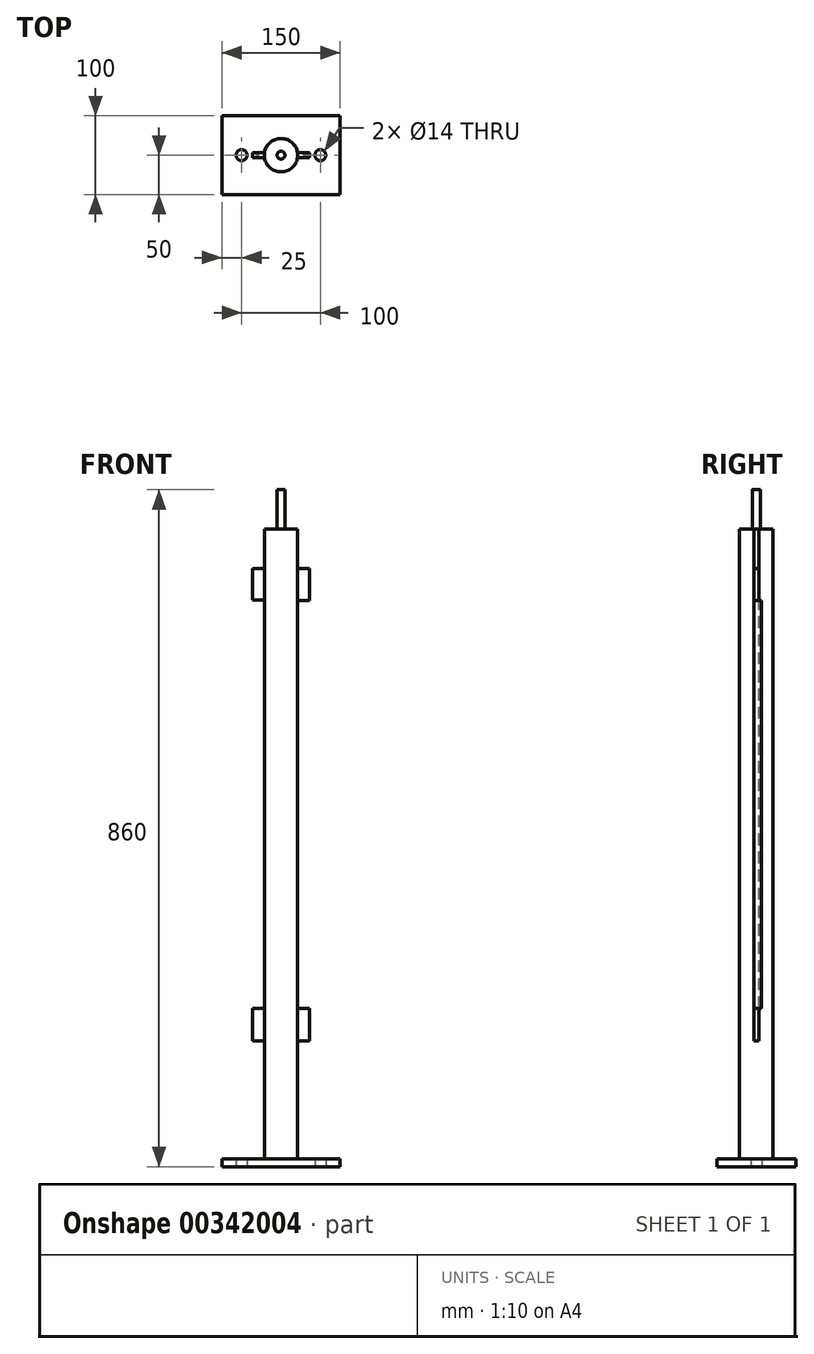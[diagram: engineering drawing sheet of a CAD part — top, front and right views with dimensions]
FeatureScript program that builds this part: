
annotation { "Feature Type Name" : "Feature", "Feature Type Description" : "" }
export const myFeature = defineFeature(function(context is Context, id is Id, definition is map)
    precondition{}
    {
        {
            var Q0;
            Q0=qCreatedBy(makeId("Top.planeOp"),FACE);
            var sketch = newSketch(context, id + "F0", { "sketchPlane" : qUnion([Q0])});
            skCircle(sketch, "E0", {"center": v(0, 0) * mm, "radius": 21.2 * mm});
            skSolve(sketch);
        }
        {
            var Q0;
            Q0 = qSketchRegion(id + "F0", true);
            extrude(context, id + "F1", {"entities" : qUnion([Q0]), "depth" : 800 * mm});
        }
        {
            var Q0;
            Q0=makeQuery(id+"F1.opExtrude","CAP_FACE",FACE,{"disambiguationData":[OSD([sQuery(id+"F0.wireOp",EDGE,"E0")])],"isStart":false});
            var sketch = newSketch(context, id + "F2", { "sketchPlane" : qUnion([Q0])});
            skCircle(sketch, "E1", {"center": v(0, 0) * mm, "radius": 5 * mm});
            skSolve(sketch);
        }
        {
            var Q0;
            Q0 = qSketchRegion(id + "F2", true);
            extrude(context, id + "F3", {"entities" : qUnion([Q0]), "operationType" : NewBodyOperationType.ADD, "depth" : 50 * mm});
        }
        {
            var Q0;
            Q0=makeQuery(id+"F1.opExtrude","CAP_FACE",FACE,{"disambiguationData":[OSD([sQuery(id+"F0.wireOp",EDGE,"E0")])],"isStart":true});
            var sketch = newSketch(context, id + "F4", { "sketchPlane" : qUnion([Q0])});
            skLineSegment(sketch, "E2.bottom", {"start": v(-75, -50) * mm, "end": v(75, -50) * mm});
            skLineSegment(sketch, "E2.top", {"start": v(-75, 50) * mm, "end": v(75, 50) * mm});
            skLineSegment(sketch, "E2.left", {"start": v(-75, -50) * mm, "end": v(-75, 50) * mm});
            skLineSegment(sketch, "E2.right", {"start": v(75, -50) * mm, "end": v(75, 50) * mm});
            skPoint(sketch, "E2.middle", {"position": v(0, 0) * mm});
            skSolve(sketch);
        }
        {
            var Q0;
            Q0 = qSketchRegion(id + "F4", true);
            extrude(context, id + "F5", {"entities" : qUnion([Q0]), "operationType" : NewBodyOperationType.ADD, "depth" : 10 * mm});
        }
        {
            var Q0;
            Q0=makeQuery(id+"F5.opExtrude","CAP_FACE",FACE,{"disambiguationData":[OSD([sQuery(id+"F4.wireOp",EDGE,"E2.bottom"),sQuery(id+"F4.wireOp",EDGE,"E2.top"),sQuery(id+"F4.wireOp",EDGE,"E2.left"),sQuery(id+"F4.wireOp",EDGE,"E2.right")])],"isStart":false});
            var sketch = newSketch(context, id + "F6", { "sketchPlane" : qUnion([Q0])});
            skLineSegment(sketch, "E3", {"start": v(-75, 0) * mm, "end": v(-50, 0) * mm});
            skLineSegment(sketch, "E4", {"start": v(75, 0) * mm, "end": v(50, 0) * mm});
            skPoint(sketch, "E4.endSnap0", {"position": v(75, 0) * mm});
            skSolve(sketch);
        }
        {
            var Q0;
            Q0=sQuery(id+"F6.wireOp",VERTEX,"E3.end");
            var Q1;
            Q1=sQuery(id+"F6.wireOp",VERTEX,"E4.end");
            var Q2;
            Q2=makeQuery(id+"F1.opExtrude","SWEPT_BODY",BODY,{"disambiguationData":[OSD([sQuery(id+"F0.wireOp",EDGE,"E0")])]});
            hole(context, id + "F7", {"style" : HoleStyle.SIMPLE, "endStyle" : HoleEndStyle.THROUGH, "holeDiameter" : 14 * mm, "isTappedThrough" : true, "tappedDepth" : 12 * mm, "tapClearance" : 3, "locations" : qUnion([Q0, Q1]), "scope" : qUnion([Q2])});
        }
        {
            var Q0;
            Q0=makeQuery(id+"F1.opExtrude","CAP_FACE",FACE,{"disambiguationData":[OSD([sQuery(id+"F0.wireOp",EDGE,"E0")])],"isStart":false});
            var sketch = newSketch(context, id + "F8", { "sketchPlane" : qUnion([Q0])});
            skLineSegment(sketch, "E5", {"start": v(36.2, 0) * mm, "end": v(36.2, 3) * mm});
            skLineSegment(sketch, "E6", {"start": v(36.2, 3) * mm, "end": v(20.99, 3) * mm});
            skLineSegment(sketch, "E7", {"start": v(36.2, 0) * mm, "end": v(36.2, -3) * mm});
            skLineSegment(sketch, "E8", {"start": v(36.2, -3) * mm, "end": v(20.99, -3) * mm});
            skLineSegment(sketch, "E9", {"start": v(20.99, -3) * mm, "end": v(20.99, 3) * mm});
            skLineSegment(sketch, "E10", {"start": v(-36.2, 0) * mm, "end": v(-36.2, 3) * mm});
            skLineSegment(sketch, "E11", {"start": v(-36.2, 3) * mm, "end": v(-20.99, 3) * mm});
            skLineSegment(sketch, "E12", {"start": v(-36.2, 0) * mm, "end": v(-36.2, -3) * mm});
            skLineSegment(sketch, "E13", {"start": v(-36.2, -3) * mm, "end": v(-20.99, -3) * mm});
            skLineSegment(sketch, "E14", {"start": v(-20.99, -3) * mm, "end": v(-20.99, 3) * mm});
            skSolve(sketch);
        }
        {
            var Q0;
            Q0 = qSketchRegion(id + "F8", true);
            extrude(context, id + "F9", {"entities" : qUnion([Q0]), "operationType" : NewBodyOperationType.ADD, "oppositeDirection" : true, "depth" : 650 * mm});
        }
        {
            var Q0;
            Q0=makeQuery(id+"F9.opExtrude","SWEPT_FACE",FACE,{"disambiguationData":[OSD([sQuery(id+"F8.wireOp",EDGE,"E13")])]});
            var sketch = newSketch(context, id + "F10", { "sketchPlane" : qUnion([Q0])});
            skLineSegment(sketch, "E15.bottom", {"start": v(-20.99, 800) * mm, "end": v(-39.72, 800) * mm});
            skLineSegment(sketch, "E15.top", {"start": v(-20.99, 750) * mm, "end": v(-39.72, 750) * mm});
            skLineSegment(sketch, "E15.left", {"start": v(-20.99, 800) * mm, "end": v(-20.99, 750) * mm});
            skLineSegment(sketch, "E15.right", {"start": v(-39.72, 800) * mm, "end": v(-39.72, 750) * mm});
            skPoint(sketch, "E16.oppositeSnap0", {"position": v(-30.35, 750) * mm});
            skLineSegment(sketch, "E16.bottom", {"start": v(21.1, 800) * mm, "end": v(39.26, 800) * mm});
            skLineSegment(sketch, "E16.top", {"start": v(21.1, 750) * mm, "end": v(39.26, 750) * mm});
            skLineSegment(sketch, "E16.left", {"start": v(21.1, 800) * mm, "end": v(21.1, 750) * mm});
            skLineSegment(sketch, "E16.right", {"start": v(39.26, 800) * mm, "end": v(39.26, 750) * mm});
            skSolve(sketch);
        }
        {
            var Q0;
            Q0 = qSketchRegion(id + "F10", true);
            extrude(context, id + "F11", {"entities" : qUnion([Q0]), "operationType" : NewBodyOperationType.REMOVE, "oppositeDirection" : true, "depth" : 25 * mm});
        }
        {
            var Q0;
            Q0=makeQuery(id+"F9.opExtrude","SWEPT_FACE",FACE,{"disambiguationData":[OSD([sQuery(id+"F8.wireOp",EDGE,"E13")])]});
            var sketch = newSketch(context, id + "F12", { "sketchPlane" : qUnion([Q0])});
            skLineSegment(sketch, "E17", {"start": v(-36.2, 750) * mm, "end": v(-36.2, 710) * mm});
            skLineSegment(sketch, "E18", {"start": v(39.25, 749.42) * mm, "end": v(39.25, 709.42) * mm});
            skLineSegment(sketch, "E19", {"start": v(-36.2, 150) * mm, "end": v(-36.2, 190) * mm});
            skLineSegment(sketch, "E20", {"start": v(36.76, 150.91) * mm, "end": v(36.76, 190.91) * mm});
            skLineSegment(sketch, "E21.bottom", {"start": v(-36.2, 710) * mm, "end": v(-20.99, 710) * mm});
            skLineSegment(sketch, "E21.top", {"start": v(-36.2, 191.23) * mm, "end": v(-20.99, 191.23) * mm});
            skLineSegment(sketch, "E21.left", {"start": v(-36.2, 710) * mm, "end": v(-36.2, 191.23) * mm});
            skLineSegment(sketch, "E21.right", {"start": v(-20.99, 710) * mm, "end": v(-20.99, 191.23) * mm});
            skLineSegment(sketch, "E22.bottom", {"start": v(39.25, 709.42) * mm, "end": v(20.16, 709.42) * mm});
            skLineSegment(sketch, "E22.top", {"start": v(39.25, 190.91) * mm, "end": v(20.16, 190.91) * mm});
            skLineSegment(sketch, "E22.left", {"start": v(39.25, 709.42) * mm, "end": v(39.25, 190.91) * mm});
            skLineSegment(sketch, "E22.right", {"start": v(20.16, 709.42) * mm, "end": v(20.16, 190.91) * mm});
            skSolve(sketch);
        }
        {
            var Q0;
            Q0 = qSketchRegion(id + "F12", true);
            extrude(context, id + "F13", {"entities" : qUnion([Q0]), "operationType" : NewBodyOperationType.REMOVE, "oppositeDirection" : true, "depth" : 25 * mm});
        }
    });
